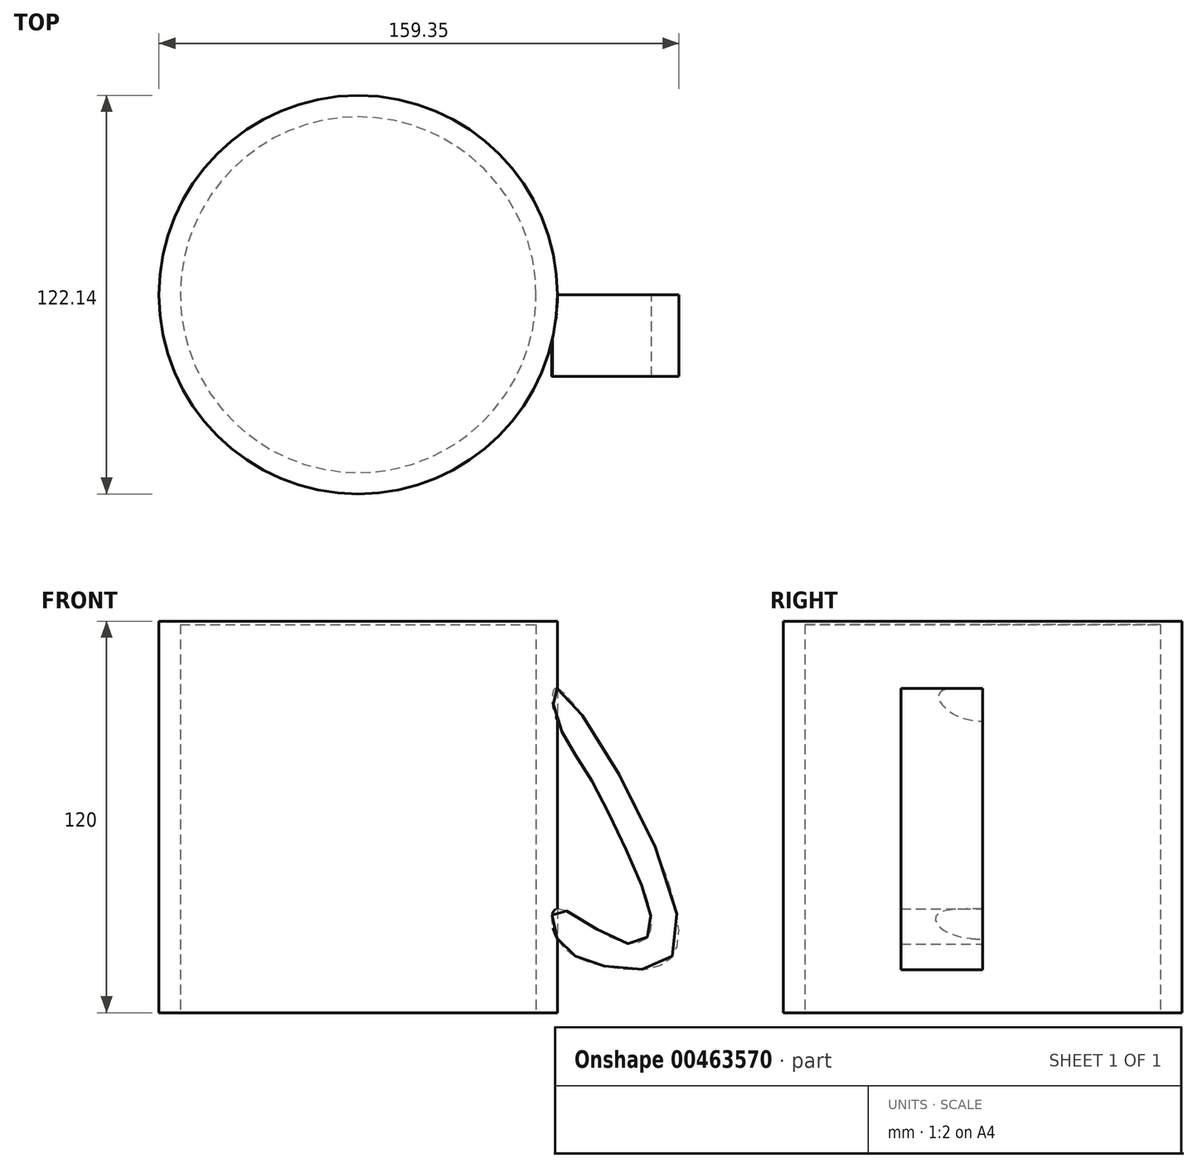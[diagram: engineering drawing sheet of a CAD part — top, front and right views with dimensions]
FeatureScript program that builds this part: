
annotation { "Feature Type Name" : "Feature", "Feature Type Description" : "" }
export const myFeature = defineFeature(function(context is Context, id is Id, definition is map)
    precondition{}
    {
        {
            var Q0;
            Q0=qCreatedBy(makeId("Top.planeOp"),FACE);
            var sketch = newSketch(context, id + "F0", { "sketchPlane" : qUnion([Q0])});
            skCircle(sketch, "E0", {"center": v(0, 0) * mm, "radius": 61.07 * mm});
            skSolve(sketch);
        }
        {
            var Q0;
            Q0 = qSketchRegion(id + "F0", true);
            extrude(context, id + "F1", {"entities" : qUnion([Q0]), "depth" : 120 * mm});
        }
        {
            var Q0;
            Q0=makeQuery(id+"F1.opExtrude","CAP_FACE",FACE,{"disambiguationData":[OSD([sQuery(id+"F0.wireOp",EDGE,"E0")])],"isStart":true});
            var sketch = newSketch(context, id + "F2", { "sketchPlane" : qUnion([Q0])});
            skCircle(sketch, "E1", {"center": v(0, 0) * mm, "radius": 54.52 * mm});
            skSolve(sketch);
        }
        {
            var Q0;
            Q0=makeQuery(id+"F2.imprint","IMPRINT",FACE,{"disambiguationData":[TD([[makeQuery(id+"F2.imprint","IMPRINT",EDGE,{"derivedFrom":sQuery(id+"F2.wireOp",EDGE,"E1")}),1.0]])]});
            extrude(context, id + "F3", {"entities" : qUnion([Q0]), "operationType" : NewBodyOperationType.REMOVE, "oppositeDirection" : true, "depth" : 119 * mm});
        }
        {
            var Q0;
            Q0=qCreatedBy(makeId("Front.planeOp"),FACE);
            var sketch = newSketch(context, id + "F4", { "sketchPlane" : qUnion([Q0])});
            skFitSpline(sketch, "E2", {"points": [v(60.95, 22.75) * mm, v(76.1, 14.2) * mm, v(98.05, 21.66) * mm, v(60.95, 99.36) * mm, v(60.95, 89.7) * mm, v(69.51, 74.56) * mm, v(84.22, 45.14) * mm, v(89.5, 24.95) * mm, v(81.37, 21.44) * mm, v(60.73, 31.75) * mm, v(60.95, 22.75) * mm]});
            skSolve(sketch);
        }
        {
            var Q0;
            Q0=makeQuery(id+"F4.imprint","IMPRINT",FACE,{"disambiguationData":[TD([[makeQuery(id+"F4.imprint","IMPRINT",EDGE,{"derivedFrom":sQuery(id+"F4.wireOp",EDGE,"E2")}),1.0]])]});
            extrude(context, id + "F5", {"entities" : qUnion([Q0]), "operationType" : NewBodyOperationType.ADD, "depth" : 25 * mm});
        }
    });
